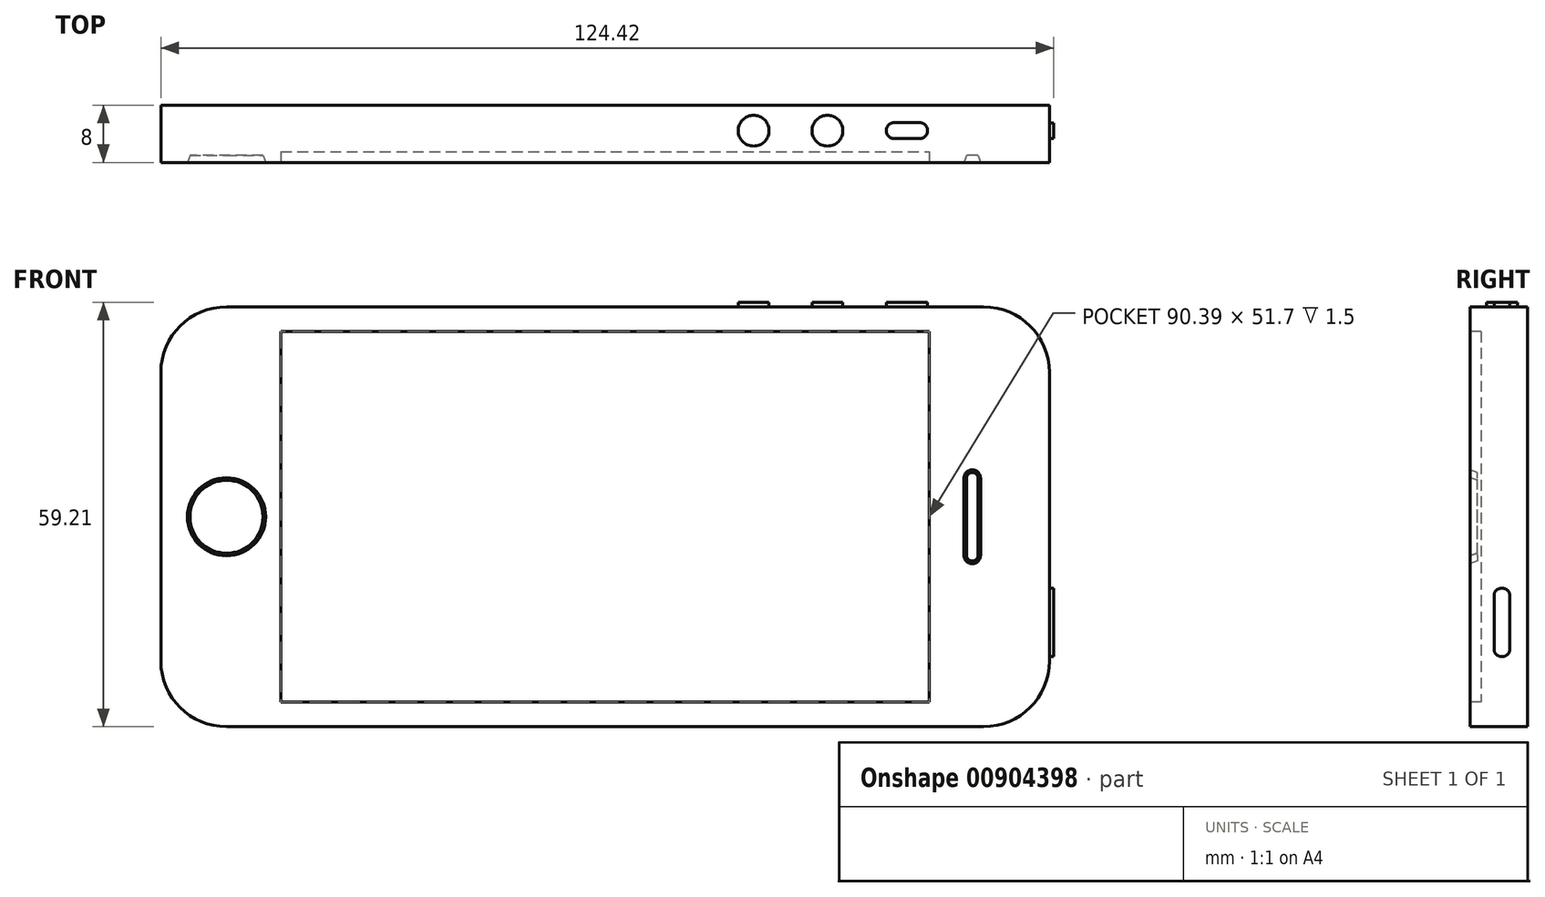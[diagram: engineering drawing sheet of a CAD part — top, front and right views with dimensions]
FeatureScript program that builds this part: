
annotation { "Feature Type Name" : "Feature", "Feature Type Description" : "" }
export const myFeature = defineFeature(function(context is Context, id is Id, definition is map)
    precondition{}
    {
        {
            var Q0;
            Q0=qCreatedBy(makeId("Front.planeOp"),FACE);
            var sketch = newSketch(context, id + "F0", { "sketchPlane" : qUnion([Q0])});
            skLineSegment(sketch, "E0.bottom", {"start": v(-52.75, -29.28) * mm, "end": v(52.75, -29.28) * mm});
            skLineSegment(sketch, "E0.top", {"start": v(-52.75, 29.29) * mm, "end": v(52.75, 29.29) * mm});
            skLineSegment(sketch, "E0.left", {"start": v(-61.91, -20.12) * mm, "end": v(-61.91, 20.13) * mm});
            skLineSegment(sketch, "E0.right", {"start": v(61.92, -20.12) * mm, "end": v(61.91, 20.13) * mm});
            skPoint(sketch, "E1.visualSharp", {"position": v(-61.91, 29.29) * mm});
            skArc(sketch, "E1.filletArc", {"start": v(-52.75, 29.29) * mm, "mid": v(-59.23, 26.6) * mm, "end": v(-61.91, 20.13) * mm});
            skPoint(sketch, "E2.visualSharp", {"position": v(-61.91, -29.28) * mm});
            skPoint(sketch, "E3.visualSharp", {"position": v(61.92, -29.28) * mm});
            skArc(sketch, "E3.filletArc", {"start": v(52.75, -29.28) * mm, "mid": v(59.23, -26.6) * mm, "end": v(61.91, -20.12) * mm});
            skPoint(sketch, "E4.visualSharp", {"position": v(61.91, 29.29) * mm});
            skArc(sketch, "E4.filletArc", {"start": v(61.91, 20.13) * mm, "mid": v(59.23, 26.6) * mm, "end": v(52.75, 29.29) * mm});
            skArc(sketch, "E5.filletArc", {"start": v(-61.91, -20.12) * mm, "mid": v(-59.23, -26.6) * mm, "end": v(-52.75, -29.28) * mm});
            skSolve(sketch);
        }
        {
            var Q0;
            Q0 = qSketchRegion(id + "F0", true);
            extrude(context, id + "F1", {"entities" : qUnion([Q0]), "oppositeDirection" : true, "depth" : 8 * mm, "offsetDistance" : 25 * mm});
        }
        {
            var Q0;
            Q0=makeQuery(id+"F1.opExtrude","CAP_FACE",FACE,{"disambiguationData":[OSD([sQuery(id+"F0.wireOp",EDGE,"E0.bottom"),sQuery(id+"F0.wireOp",EDGE,"E0.top"),sQuery(id+"F0.wireOp",EDGE,"E0.left"),sQuery(id+"F0.wireOp",EDGE,"E0.right"),sQuery(id+"F0.wireOp",EDGE,"E1.filletArc"),sQuery(id+"F0.wireOp",EDGE,"E2.filletArc"),sQuery(id+"F0.wireOp",EDGE,"E3.filletArc"),sQuery(id+"F0.wireOp",EDGE,"E4.filletArc")])],"isStart":true});
            var sketch = newSketch(context, id + "F2", { "sketchPlane" : qUnion([Q0])});
            skCircle(sketch, "E6", {"center": v(-52.76, 0) * mm, "radius": 5.45 * mm});
            skSolve(sketch);
        }
        {
            var Q0;
            Q0 = qSketchRegion(id + "F2", true);
            extrude(context, id + "F3", {"entities" : qUnion([Q0]), "operationType" : NewBodyOperationType.REMOVE, "oppositeDirection" : true, "depth" : 1 * mm, "offsetDistance" : 25 * mm, "hasDraft" : true, "draftAngle" : 20 * degree, "draftPullDirection" : true});
        }
        {
            var Q0;
            Q0=makeQuery(id+"F1.opExtrude","CAP_FACE",FACE,{"disambiguationData":[OSD([sQuery(id+"F0.wireOp",EDGE,"E0.bottom"),sQuery(id+"F0.wireOp",EDGE,"E0.top"),sQuery(id+"F0.wireOp",EDGE,"E0.left"),sQuery(id+"F0.wireOp",EDGE,"E0.right"),sQuery(id+"F0.wireOp",EDGE,"E1.filletArc"),sQuery(id+"F0.wireOp",EDGE,"E2.filletArc"),sQuery(id+"F0.wireOp",EDGE,"E3.filletArc"),sQuery(id+"F0.wireOp",EDGE,"E4.filletArc")])],"isStart":true});
            var sketch = newSketch(context, id + "F4", { "sketchPlane" : qUnion([Q0])});
            skLineSegment(sketch, "E7", {"start": v(51.16, 5.4) * mm, "end": v(51.16, -5.4) * mm});
            skArc(sketch, "E8.0.startCap", {"start": v(50.01, 5.4) * mm, "mid": v(51.16, 6.55) * mm, "end": v(52.31, 5.4) * mm});
            skArc(sketch, "E8.0.endCap", {"start": v(52.31, -5.4) * mm, "mid": v(51.16, -6.55) * mm, "end": v(50.01, -5.4) * mm});
            skLineSegment(sketch, "E8.0.left", {"start": v(52.31, 5.4) * mm, "end": v(52.31, -5.4) * mm});
            skLineSegment(sketch, "E8.0.right", {"start": v(50.01, 5.4) * mm, "end": v(50.01, -5.4) * mm});
            skSolve(sketch);
        }
        {
            var Q0;
            Q0 = qSketchRegion(id + "F4", true);
            extrude(context, id + "F5", {"entities" : qUnion([Q0]), "operationType" : NewBodyOperationType.REMOVE, "oppositeDirection" : true, "depth" : 1 * mm, "offsetDistance" : 25 * mm, "hasDraft" : true, "draftAngle" : 20 * degree, "draftPullDirection" : true});
        }
        {
            var Q0;
            Q0=makeQuery(id+"F1.opExtrude","SWEPT_FACE",FACE,{"disambiguationData":[OSD([sQuery(id+"F0.wireOp",EDGE,"E0.top")])]});
            var sketch = newSketch(context, id + "F6", { "sketchPlane" : qUnion([Q0])});
            skCircle(sketch, "E9", {"center": v(20.7, 4.44) * mm, "radius": 2.15 * mm});
            skCircle(sketch, "E10", {"center": v(30.98, 4.44) * mm, "radius": 2.15 * mm});
            skLineSegment(sketch, "E11.bottom", {"start": v(40.2, 5.55) * mm, "end": v(43.9, 5.55) * mm});
            skLineSegment(sketch, "E11.top", {"start": v(40.2, 3.35) * mm, "end": v(43.9, 3.35) * mm});
            skLineSegment(sketch, "E11.left", {"start": v(39.2, 4.55) * mm, "end": v(39.2, 4.35) * mm});
            skLineSegment(sketch, "E11.right", {"start": v(44.9, 4.55) * mm, "end": v(44.9, 4.35) * mm});
            skPoint(sketch, "E12.visualSharp", {"position": v(39.2, 5.55) * mm});
            skArc(sketch, "E12.filletArc", {"start": v(40.2, 5.55) * mm, "mid": v(39.5, 5.26) * mm, "end": v(39.2, 4.55) * mm});
            skPoint(sketch, "E13.visualSharp", {"position": v(39.2, 3.35) * mm});
            skArc(sketch, "E13.filletArc", {"start": v(39.2, 4.35) * mm, "mid": v(39.5, 3.64) * mm, "end": v(40.2, 3.35) * mm});
            skPoint(sketch, "E14.visualSharp", {"position": v(44.9, 3.35) * mm});
            skArc(sketch, "E14.filletArc", {"start": v(43.9, 3.35) * mm, "mid": v(44.61, 3.64) * mm, "end": v(44.9, 4.35) * mm});
            skPoint(sketch, "E15.visualSharp", {"position": v(44.9, 5.55) * mm});
            skArc(sketch, "E15.filletArc", {"start": v(44.9, 4.55) * mm, "mid": v(44.61, 5.26) * mm, "end": v(43.9, 5.55) * mm});
            skSolve(sketch);
        }
        {
            var Q0;
            Q0 = qSketchRegion(id + "F6", true);
            extrude(context, id + "F7", {"entities" : qUnion([Q0]), "operationType" : NewBodyOperationType.ADD, "depth" : 0.63 * mm, "offsetDistance" : 25 * mm});
        }
        {
            var Q0;
            Q0=makeQuery(id+"F1.opExtrude","CAP_FACE",FACE,{"disambiguationData":[OSD([sQuery(id+"F0.wireOp",EDGE,"E0.bottom"),sQuery(id+"F0.wireOp",EDGE,"E0.top"),sQuery(id+"F0.wireOp",EDGE,"E0.left"),sQuery(id+"F0.wireOp",EDGE,"E0.right"),sQuery(id+"F0.wireOp",EDGE,"E1.filletArc"),sQuery(id+"F0.wireOp",EDGE,"E2.filletArc"),sQuery(id+"F0.wireOp",EDGE,"E3.filletArc"),sQuery(id+"F0.wireOp",EDGE,"E4.filletArc")])],"isStart":true});
            var sketch = newSketch(context, id + "F8", { "sketchPlane" : qUnion([Q0])});
            skLineSegment(sketch, "E16.bottom", {"start": v(-45.2, 25.85) * mm, "end": v(45.2, 25.85) * mm});
            skLineSegment(sketch, "E16.top", {"start": v(-45.2, -25.85) * mm, "end": v(45.2, -25.85) * mm});
            skLineSegment(sketch, "E16.left", {"start": v(-45.2, 25.85) * mm, "end": v(-45.2, -25.85) * mm});
            skLineSegment(sketch, "E16.right", {"start": v(45.2, 25.85) * mm, "end": v(45.2, -25.85) * mm});
            skSolve(sketch);
        }
        {
            var Q0;
            Q0 = qSketchRegion(id + "F8", true);
            extrude(context, id + "F9", {"entities" : qUnion([Q0]), "operationType" : NewBodyOperationType.REMOVE, "oppositeDirection" : true, "depth" : 1.5 * mm, "offsetDistance" : 25 * mm});
        }
        {
            var Q0;
            Q0=makeQuery(id+"F1.opExtrude","SWEPT_FACE",FACE,{"disambiguationData":[OSD([sQuery(id+"F0.wireOp",EDGE,"E0.right")])]});
            var sketch = newSketch(context, id + "F10", { "sketchPlane" : qUnion([Q0])});
            skLineSegment(sketch, "E17.bottom", {"start": v(4.34, -9.98) * mm, "end": v(4.54, -9.98) * mm});
            skLineSegment(sketch, "E17.top", {"start": v(4.34, -19.48) * mm, "end": v(4.54, -19.48) * mm});
            skLineSegment(sketch, "E17.left", {"start": v(3.34, -10.98) * mm, "end": v(3.34, -18.48) * mm});
            skLineSegment(sketch, "E17.right", {"start": v(5.54, -10.98) * mm, "end": v(5.54, -18.48) * mm});
            skPoint(sketch, "E18.visualSharp", {"position": v(3.34, -9.98) * mm});
            skArc(sketch, "E18.filletArc", {"start": v(4.34, -9.98) * mm, "mid": v(3.63, -10.28) * mm, "end": v(3.34, -10.98) * mm});
            skPoint(sketch, "E19.visualSharp", {"position": v(5.54, -19.48) * mm});
            skArc(sketch, "E19.filletArc", {"start": v(4.54, -19.48) * mm, "mid": v(5.25, -19.2) * mm, "end": v(5.54, -18.48) * mm});
            skPoint(sketch, "E20.visualSharp", {"position": v(5.54, -9.98) * mm});
            skArc(sketch, "E20.filletArc", {"start": v(5.54, -10.98) * mm, "mid": v(5.25, -10.28) * mm, "end": v(4.54, -9.98) * mm});
            skPoint(sketch, "E21.visualSharp", {"position": v(3.34, -19.48) * mm});
            skArc(sketch, "E21.filletArc", {"start": v(3.34, -18.48) * mm, "mid": v(3.63, -19.2) * mm, "end": v(4.34, -19.48) * mm});
            skSolve(sketch);
        }
        {
            var Q0;
            Q0 = qSketchRegion(id + "F10", true);
            extrude(context, id + "F11", {"entities" : qUnion([Q0]), "operationType" : NewBodyOperationType.ADD, "depth" : 0.58 * mm, "offsetDistance" : 25 * mm});
        }
    });
